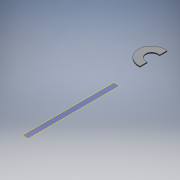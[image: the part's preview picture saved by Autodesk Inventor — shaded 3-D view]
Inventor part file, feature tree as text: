
AUTODESK INVENTOR PART (.ipt)
format: ipt  version: 2018 (Build 220112000, 112)  size: 118,272 bytes
history: native  units: mm
features: other x5, reference x2, plane x1, sheet_metal_op x1, sketch x1
ambient origin geometry x8: Origin, YZ Plane, XZ Plane, XY Plane, X Axis, Y Axis, Z Axis, Center Point
bodies: Solid1 (feature_tree)
feature tree (10):
  plane  "Work Plane1"
  sheet_metal_op  "Face1"
  sketch  "Sketch1"  dims[d0=30.0mm d1=6.0mm d2=4.0mm]
  reference  "Reference1"
  reference  "Reference2"
  other  "Plate1"
  other  "<path>, oppe, top.iam"
  other  "hegnspæl, oppe, top.iam"
  other  "Frame0002:1"
  other  "DIN T30 00000001:1"
note: 1 file-system path scrubbed to <path> (originals preserved in map.json)
